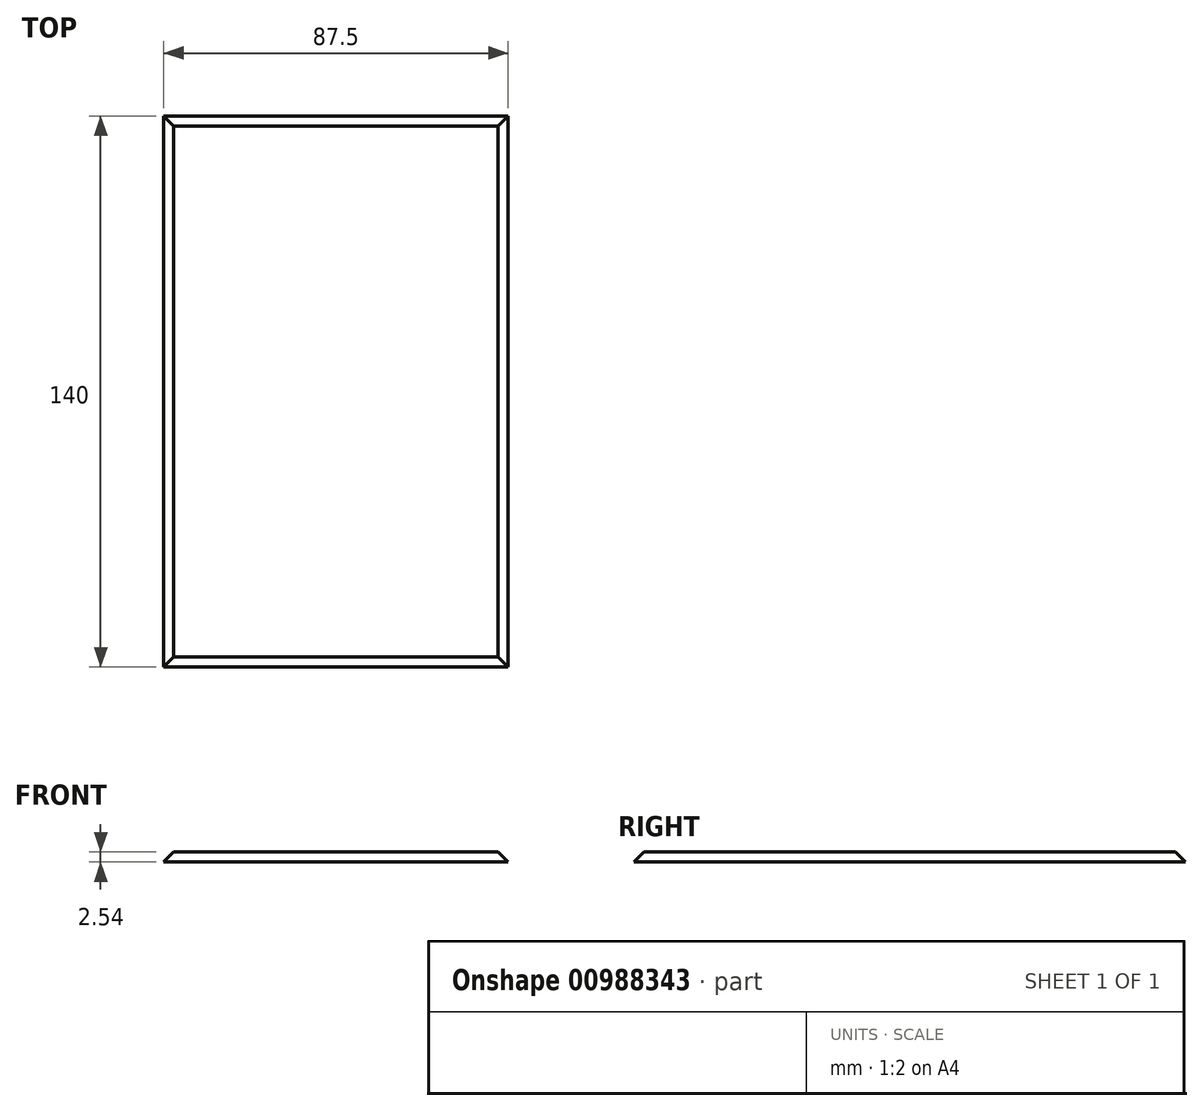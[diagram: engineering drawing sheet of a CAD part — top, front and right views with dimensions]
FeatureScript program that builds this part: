
annotation { "Feature Type Name" : "Feature", "Feature Type Description" : "" }
export const myFeature = defineFeature(function(context is Context, id is Id, definition is map)
    precondition{}
    {
        {
            var Q0;
            Q0=qCreatedBy(makeId("Top.planeOp"),FACE);
            var sketch = newSketch(context, id + "F0", { "sketchPlane" : qUnion([Q0])});
            skLineSegment(sketch, "E0.bottom", {"start": v(43.75, 70) * mm, "end": v(-43.75, 70) * mm});
            skLineSegment(sketch, "E0.top", {"start": v(43.75, -70) * mm, "end": v(-43.75, -70) * mm});
            skLineSegment(sketch, "E0.left", {"start": v(43.75, 70) * mm, "end": v(43.75, -70) * mm});
            skLineSegment(sketch, "E0.right", {"start": v(-43.75, 70) * mm, "end": v(-43.75, -70) * mm});
            skPoint(sketch, "E0.middle", {"position": v(0, 0) * mm});
            skSolve(sketch);
        }
        {
            var Q0;
            Q0=makeQuery(id+"F0.imprint","IMPRINT",FACE,{"disambiguationData":[TD([[makeQuery(id+"F0.imprint","IMPRINT",EDGE,{"derivedFrom":sQuery(id+"F0.wireOp",EDGE,"E0.bottom")}),1.0]])]});
            extrude(context, id + "F1", {"entities" : qUnion([Q0]), "depth" : 2.54 * mm, "offsetDistance" : 25.4 * mm});
        }
        {
            var Q0;
            Q0=makeQuery(id+"F1.opExtrude","CAP_EDGE",EDGE,{"disambiguationData":[OSD([sQuery(id+"F0.wireOp",EDGE,"E0.left")])],"isStart":false});
            var Q1;
            Q1=makeQuery(id+"F1.opExtrude","CAP_EDGE",EDGE,{"disambiguationData":[OSD([sQuery(id+"F0.wireOp",EDGE,"E0.right")])],"isStart":false});
            var Q2;
            Q2=makeQuery(id+"F1.opExtrude","CAP_EDGE",EDGE,{"disambiguationData":[OSD([sQuery(id+"F0.wireOp",EDGE,"E0.bottom")])],"isStart":false});
            var Q3;
            Q3=makeQuery(id+"F1.opExtrude","CAP_EDGE",EDGE,{"disambiguationData":[OSD([sQuery(id+"F0.wireOp",EDGE,"E0.top")])],"isStart":false});
            chamfer(context, id + "F2", {"entities" : qUnion([Q0, Q1, Q2, Q3]), "width" : 2.54 * mm, "tangentPropagation" : true});
        }
    });
